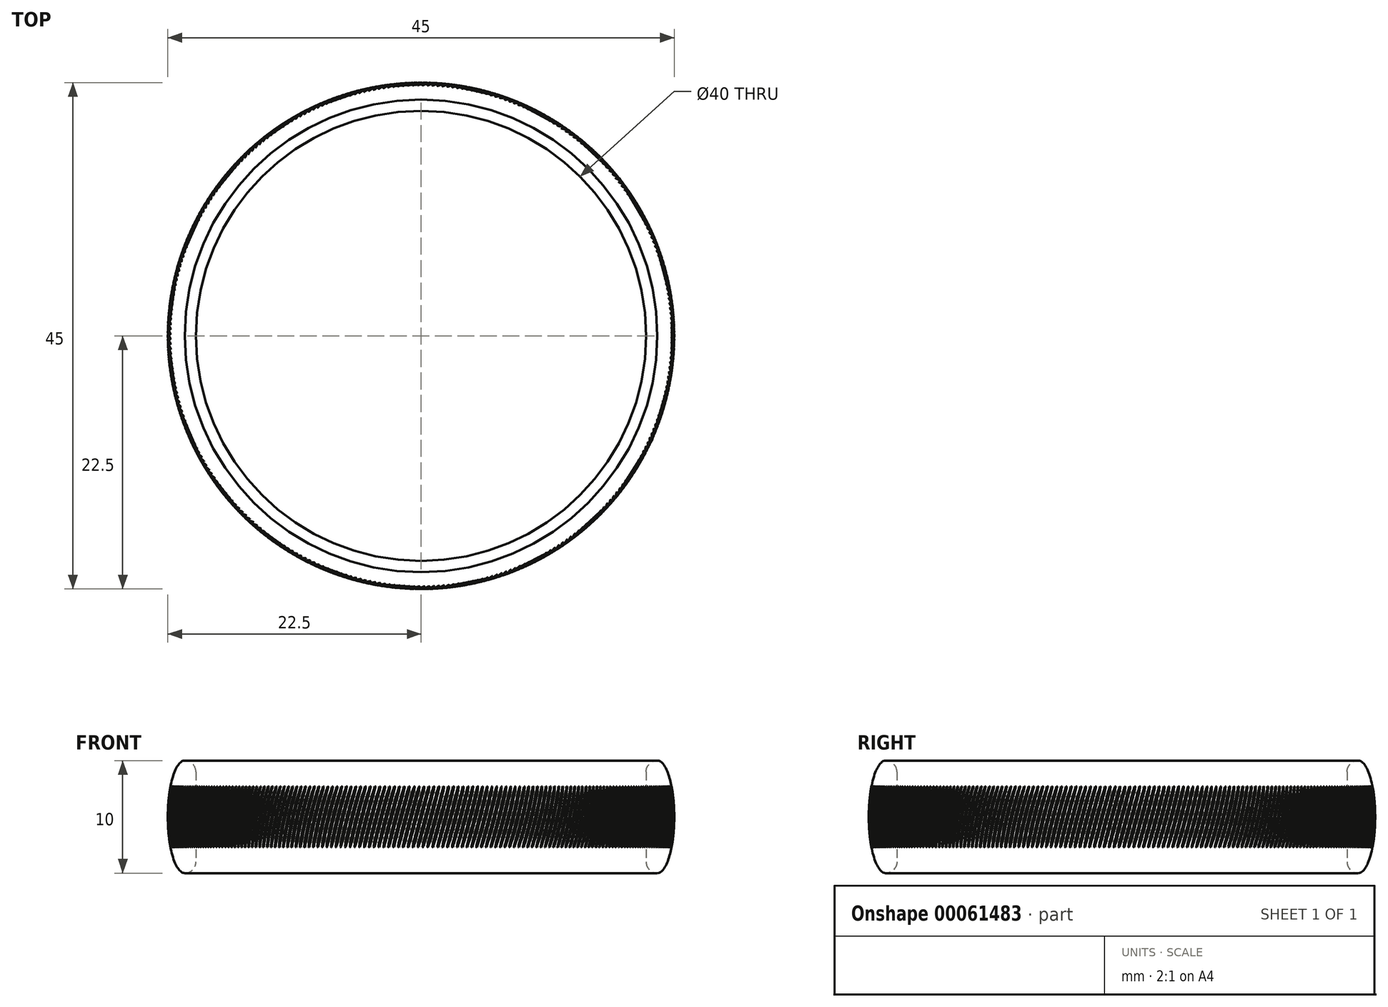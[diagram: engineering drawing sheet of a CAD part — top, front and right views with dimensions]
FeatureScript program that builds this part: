
annotation { "Feature Type Name" : "Feature", "Feature Type Description" : "" }
export const myFeature = defineFeature(function(context is Context, id is Id, definition is map)
    precondition{}
    {
        {
            var Q0;
            Q0=qCreatedBy(makeId("Front.planeOp"),FACE);
            var sketch = newSketch(context, id + "F0", { "sketchPlane" : qUnion([Q0])});
            skLineSegment(sketch, "E0", {"start": v(-20, 0) * mm, "end": v(-20, 27.16) * mm});
            skLineSegment(sketch, "E1.left", {"start": v(0, 4) * mm, "end": v(0, -4) * mm});
            skPoint(sketch, "E2.visualSharp", {"position": v(0, 5) * mm});
            skArc(sketch, "E2.filletArc", {"start": v(1, 5) * mm, "mid": v(0.3, 4.7) * mm, "end": v(0, 4) * mm});
            skPoint(sketch, "E3.visualSharp", {"position": v(0, -5) * mm});
            skArc(sketch, "E3.filletArc", {"start": v(0, -4) * mm, "mid": v(0.3, -4.7) * mm, "end": v(1, -5) * mm});
            skEllipticalArc(sketch, "E4", {});
            const initialGuessF0  = {"E4": [0.001, 0, 0, 1, 0.005, 0.0015, 3.141592653589793, 0]};
            skSetInitialGuess(sketch, initialGuessF0);
            skSolve(sketch);
        }
        {
            var Q0;
            Q0=makeQuery(id+"F0.imprint","IMPRINT",FACE,{"disambiguationData":[TD([[makeQuery(id+"F0.imprint","IMPRINT",EDGE,{"derivedFrom":sQuery(id+"F0.wireOp",EDGE,"E1.left")}),1.0]])]});
            var Q1;
            Q1=sQuery(id+"F0.wireOp",EDGE,"E0");
            revolve(context, id + "F1", {"entities" : qUnion([Q0]), "axis" : qUnion([Q1]), "revolveType" : RevolveType.FULL});
        }
        {
            var Q0;
            Q0=qCreatedBy(makeId("Front.planeOp"),FACE);
            var sketch = newSketch(context, id + "F2", { "sketchPlane" : qUnion([Q0])});
            skLineSegment(sketch, "E5", {"start": v(0, 0) * mm, "end": v(-40, 0) * mm});
            skLineSegment(sketch, "E6", {"start": v(-40, -4) * mm, "end": v(-40, 4) * mm});
            skLineSegment(sketch, "E7", {"start": v(0, 4) * mm, "end": v(0, -4) * mm});
            skLineSegment(sketch, "E8", {"start": v(-20, 0) * mm, "end": v(-20, 20.98) * mm});
            skPoint(sketch, "E8.endSnap0", {"position": v(-20, 0) * mm});
            skLineSegment(sketch, "E9", {"start": v(-20, 0) * mm, "end": v(6.07, 6.99) * mm});
            skSolve(sketch);
        }
        {
            var Q0;
            Q0=qCreatedBy(makeId("Right.planeOp"),FACE);
            var Q1;
            Q1=sQuery(id+"F2.wireOp",VERTEX,"E8.endSnap0");
            cPlane(context, id + "F3", {"entities" : qUnion([Q0, Q1]), "cplaneType" : CPlaneType.PLANE_POINT, "offset" : 25 * mm, "width" : 150 * mm, "height" : 150 * mm});
        }
        {
            var Q0;
            Q0=qCreatedBy(makeId("Top.planeOp"),FACE);
            var sketch = newSketch(context, id + "F4", { "sketchPlane" : qUnion([Q0])});
            skCircle(sketch, "E10", {"center": v(-20, 0) * mm, "radius": 22.5 * mm});
            skLineSegment(sketch, "E11", {"start": v(-20, 0) * mm, "end": v(-20, 26.25) * mm});
            skArc(sketch, "E12", {"start": v(-20.07, 22.5) * mm, "mid": v(-20, 22.43) * mm, "end": v(-19.93, 22.5) * mm});
            skSolve(sketch);
        }
        {
            var Q0;
            {var subQ0=sQuery(id+"F4.wireOp",EDGE,"E12");var subQ1=sQuery(id+"F4.wireOp",EDGE,"E10");var subQ2=makeQuery(id+"F4.imprint","INTERSECT",VERTEX,{"disambiguationData":[OD(1.0)],"derivedFrom":[subQ1,subQ0]});Q0=makeQuery(id+"F4.imprint","IMPRINT",FACE,{"disambiguationData":[TD([[makeQuery(id+"F4.imprint","IMPRINT",EDGE,{"disambiguationData":[TD([[subQ2,-1.0]])],"derivedFrom":subQ1}),1.0]])]});}
            var Q1;
            {var subQ0=sQuery(id+"F4.wireOp",EDGE,"E12");var subQ1=sQuery(id+"F4.wireOp",EDGE,"E10");var subQ2=makeQuery(id+"F4.imprint","INTERSECT",VERTEX,{"disambiguationData":[OD(0.0)],"derivedFrom":[subQ1,subQ0]});Q1=makeQuery(id+"F4.imprint","IMPRINT",FACE,{"disambiguationData":[TD([[makeQuery(id+"F4.imprint","IMPRINT",EDGE,{"disambiguationData":[TD([[subQ2,1.0]])],"derivedFrom":subQ1}),1.0]])]});}
            var Q2;
            Q2=sQuery(id+"F2.wireOp",EDGE,"E9");
            revolve(context, id + "F5", {"entities" : qUnion([Q0, Q1]), "axis" : qUnion([Q2]), "revolveType" : RevolveType.SYMMETRIC, "oppositeDirection" : true, "angle" : 30 * degree});
        }
        {
            var Q0;
            Q0=makeQuery(id+"F5.opRevolve","SWEPT_BODY",BODY,{"disambiguationData":[OSD([sQuery(id+"F4.wireOp",EDGE,"E10"),sQuery(id+"F4.wireOp",EDGE,"E12")])]});
            var Q1;
            Q1=sQuery(id+"F2.wireOp",EDGE,"E8");
            circularPattern(context, id + "F6", {"operationType" : NewBodyOperationType.REMOVE, "entities" : qUnion([Q0]), "axis" : qUnion([Q1]), "angle" : 360 * degree, "instanceCount" : 320, "equalSpace" : true});
        }
    });
